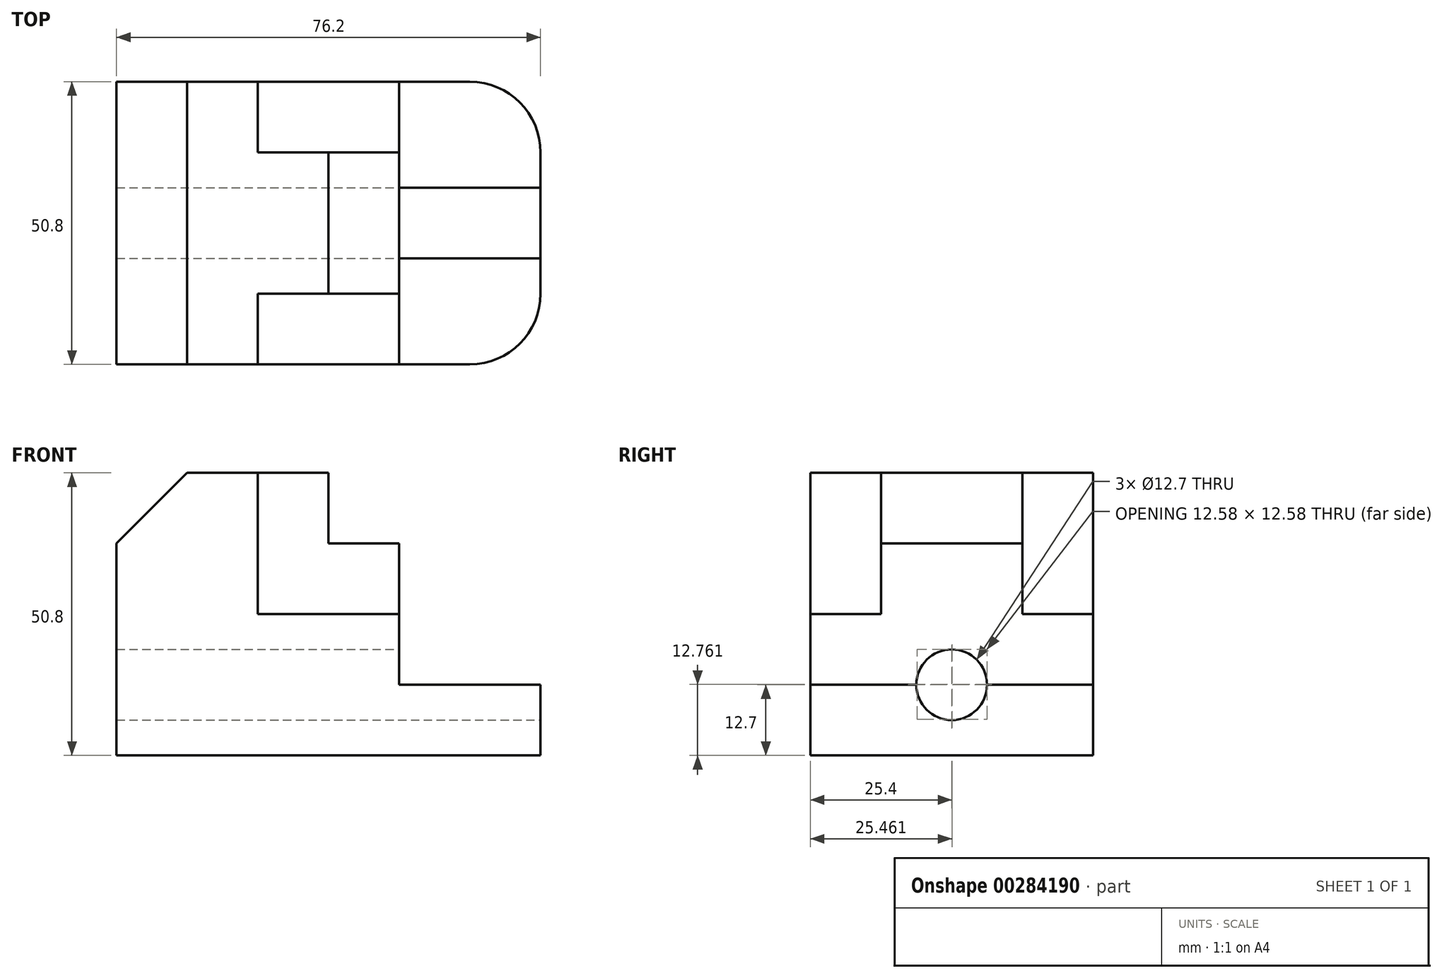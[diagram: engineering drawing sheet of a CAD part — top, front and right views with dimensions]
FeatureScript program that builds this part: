
annotation { "Feature Type Name" : "Feature", "Feature Type Description" : "" }
export const myFeature = defineFeature(function(context is Context, id is Id, definition is map)
    precondition{}
    {
        {
            var Q0;
            Q0=qCreatedBy(makeId("Front.planeOp"),FACE);
            var sketch = newSketch(context, id + "F0", { "sketchPlane" : qUnion([Q0])});
            skLineSegment(sketch, "E0", {"start": v(0, 0) * mm, "end": v(0, 38.1) * mm});
            skLineSegment(sketch, "E1", {"start": v(0, 38.1) * mm, "end": v(12.7, 50.8) * mm});
            skLineSegment(sketch, "E2", {"start": v(12.7, 50.8) * mm, "end": v(38.1, 50.8) * mm});
            skLineSegment(sketch, "E3", {"start": v(38.1, 50.8) * mm, "end": v(38.1, 38.1) * mm});
            skLineSegment(sketch, "E4", {"start": v(38.1, 38.1) * mm, "end": v(50.8, 38.1) * mm});
            skLineSegment(sketch, "E5", {"start": v(50.8, 38.1) * mm, "end": v(50.8, 12.7) * mm});
            skLineSegment(sketch, "E6", {"start": v(50.8, 12.7) * mm, "end": v(76.2, 12.7) * mm});
            skLineSegment(sketch, "E7", {"start": v(76.2, 12.7) * mm, "end": v(76.2, 0) * mm});
            skLineSegment(sketch, "E8", {"start": v(76.2, 0) * mm, "end": v(0, 0) * mm});
            skSolve(sketch);
        }
        {
            var Q0;
            Q0 = qSketchRegion(id + "F0", true);
            extrude(context, id + "F1", {"entities" : qUnion([Q0]), "depth" : 50.8 * mm});
        }
        {
            var Q0;
            Q0=makeQuery(id+"F1.opExtrude","SWEPT_FACE",FACE,{"disambiguationData":[OSD([sQuery(id+"F0.wireOp",EDGE,"E2")])]});
            var sketch = newSketch(context, id + "F2", { "sketchPlane" : qUnion([Q0])});
            skLineSegment(sketch, "E9.bottom", {"start": v(38.1, 0) * mm, "end": v(50.8, 0) * mm});
            skLineSegment(sketch, "E9.top", {"start": v(38.1, -12.7) * mm, "end": v(50.8, -12.7) * mm});
            skLineSegment(sketch, "E9.left", {"start": v(38.1, 0) * mm, "end": v(38.1, -12.7) * mm});
            skLineSegment(sketch, "E9.right", {"start": v(50.8, 0) * mm, "end": v(50.8, -12.7) * mm});
            skLineSegment(sketch, "E10.bottom", {"start": v(38.1, -50.8) * mm, "end": v(50.8, -50.8) * mm});
            skLineSegment(sketch, "E10.top", {"start": v(38.1, -38.1) * mm, "end": v(50.8, -38.1) * mm});
            skLineSegment(sketch, "E10.left", {"start": v(38.1, -50.8) * mm, "end": v(38.1, -38.1) * mm});
            skLineSegment(sketch, "E10.right", {"start": v(50.8, -50.8) * mm, "end": v(50.8, -38.1) * mm});
            skSolve(sketch);
        }
        {
            var Q0;
            Q0 = qSketchRegion(id + "F2", true);
            extrude(context, id + "F3", {"entities" : qUnion([Q0]), "operationType" : NewBodyOperationType.REMOVE, "oppositeDirection" : true, "depth" : 25.4 * mm});
        }
        {
            var Q0;
            Q0=makeQuery(id+"F1.opExtrude","SWEPT_FACE",FACE,{"disambiguationData":[OSD([sQuery(id+"F0.wireOp",EDGE,"E2")])]});
            var sketch = newSketch(context, id + "F4", { "sketchPlane" : qUnion([Q0])});
            skLineSegment(sketch, "E11.bottom", {"start": v(38.1, -12.7) * mm, "end": v(25.4, -12.7) * mm});
            skLineSegment(sketch, "E11.top", {"start": v(38.1, 0) * mm, "end": v(25.4, 0) * mm});
            skLineSegment(sketch, "E11.left", {"start": v(38.1, -12.7) * mm, "end": v(38.1, 0) * mm});
            skLineSegment(sketch, "E11.right", {"start": v(25.4, -12.7) * mm, "end": v(25.4, 0) * mm});
            skLineSegment(sketch, "E12.bottom", {"start": v(25.4, -50.8) * mm, "end": v(38.1, -50.8) * mm});
            skLineSegment(sketch, "E12.top", {"start": v(25.4, -38.1) * mm, "end": v(38.1, -38.1) * mm});
            skLineSegment(sketch, "E12.left", {"start": v(25.4, -50.8) * mm, "end": v(25.4, -38.1) * mm});
            skLineSegment(sketch, "E12.right", {"start": v(38.1, -50.8) * mm, "end": v(38.1, -38.1) * mm});
            skSolve(sketch);
        }
        {
            var Q0;
            Q0 = qSketchRegion(id + "F4", true);
            extrude(context, id + "F5", {"entities" : qUnion([Q0]), "operationType" : NewBodyOperationType.REMOVE, "oppositeDirection" : true, "depth" : 25.4 * mm});
        }
        {
            var Q0;
            Q0=makeQuery(id+"F1.opExtrude","CAP_EDGE",EDGE,{"disambiguationData":[OSD([sQuery(id+"F0.wireOp",EDGE,"E7")])],"isStart":false});
            var Q1;
            Q1=makeQuery(id+"F1.opExtrude","CAP_EDGE",EDGE,{"disambiguationData":[OSD([sQuery(id+"F0.wireOp",EDGE,"E7")])],"isStart":true});
            fillet(context, id + "F6", {"entities" : qUnion([Q0, Q1]), "radius" : 12.7 * mm, "tangentPropagation" : true, "allowEdgeOverflow" : false});
        }
        {
            var Q0;
            Q0=makeQuery(id+"F1.opExtrude","SWEPT_FACE",FACE,{"disambiguationData":[OSD([sQuery(id+"F0.wireOp",EDGE,"E7")])]});
            var sketch = newSketch(context, id + "F7", { "sketchPlane" : qUnion([Q0])});
            skCircle(sketch, "E13", {"center": v(-25.4, 12.7) * mm, "radius": 6.35 * mm});
            skSolve(sketch);
        }
        {
            var Q0;
            Q0 = qSketchRegion(id + "F7", true);
            extrude(context, id + "F8", {"entities" : qUnion([Q0]), "operationType" : NewBodyOperationType.REMOVE, "endBound" : BoundingType.THROUGH_ALL, "oppositeDirection" : true, "depth" : 25.4 * mm});
        }
    });
